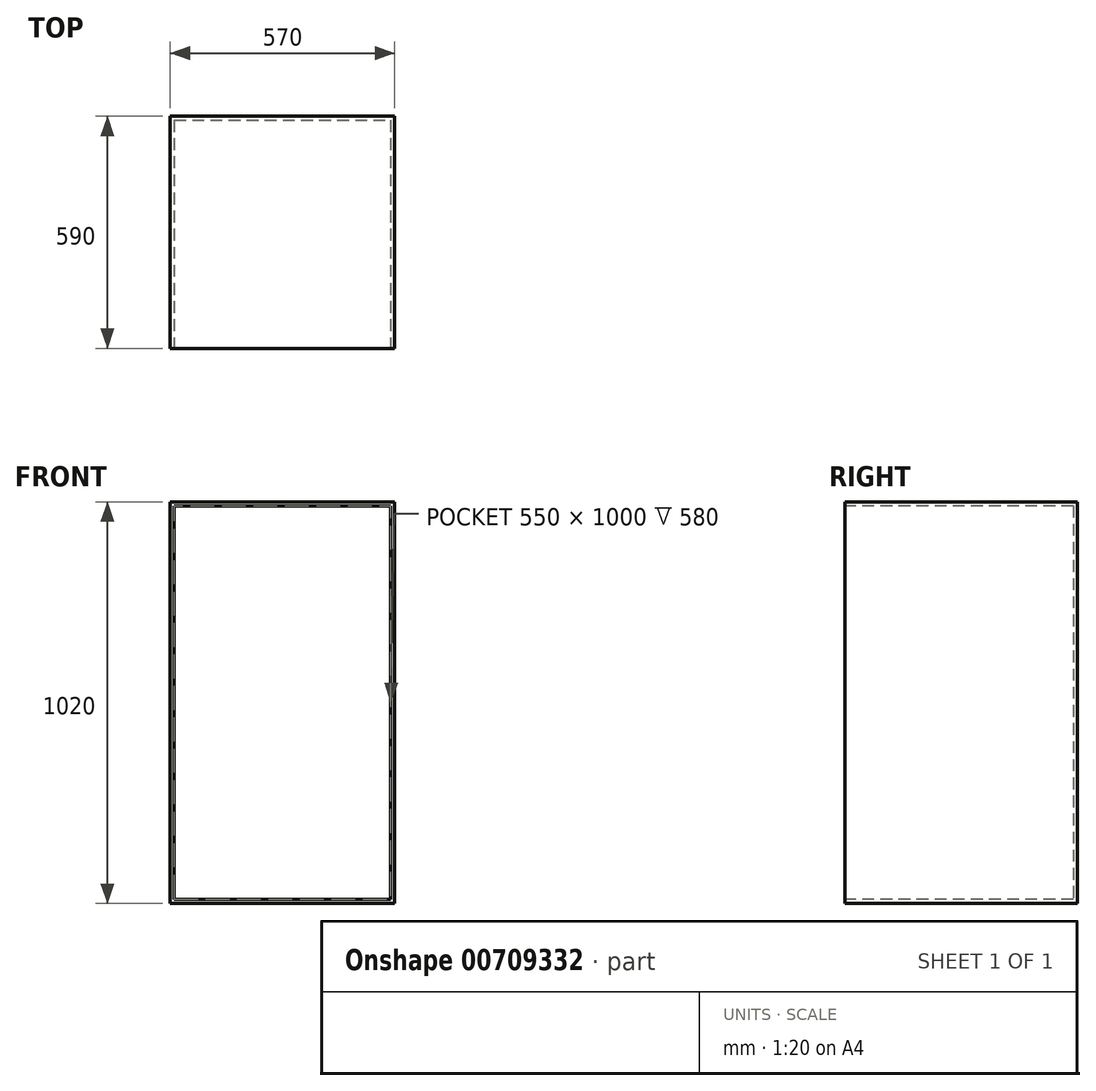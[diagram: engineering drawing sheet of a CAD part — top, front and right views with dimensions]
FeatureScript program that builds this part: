
annotation { "Feature Type Name" : "Feature", "Feature Type Description" : "" }
export const myFeature = defineFeature(function(context is Context, id is Id, definition is map)
    precondition{}
    {
        {
            var Q0;
            Q0=qCreatedBy(makeId("Top.planeOp"),FACE);
            var sketch = newSketch(context, id + "F0", { "sketchPlane" : qUnion([Q0])});
            skLineSegment(sketch, "E0.bottom", {"start": v(-275, 290) * mm, "end": v(275, 290) * mm});
            skLineSegment(sketch, "E0.top", {"start": v(-275, -290) * mm, "end": v(275, -290) * mm});
            skLineSegment(sketch, "E0.left", {"start": v(-275, 290) * mm, "end": v(-275, -290) * mm});
            skLineSegment(sketch, "E0.right", {"start": v(275, 290) * mm, "end": v(275, -290) * mm});
            skPoint(sketch, "E0.middle", {"position": v(0, 0) * mm});
            skSolve(sketch);
        }
        {
            var Q0;
            Q0=makeQuery(id+"F0.imprint","IMPRINT",FACE,{"disambiguationData":[TD([[makeQuery(id+"F0.imprint","IMPRINT",EDGE,{"derivedFrom":sQuery(id+"F0.wireOp",EDGE,"E0.bottom")}),-1.0]])]});
            extrude(context, id + "F1", {"entities" : qUnion([Q0]), "depth" : 1000 * mm, "offsetDistance" : 25 * mm});
        }
        {
            var Q0;
            Q0=makeQuery(id+"F1.opExtrude","SWEPT_FACE",FACE,{"disambiguationData":[OSD([sQuery(id+"F0.wireOp",EDGE,"E0.top")])]});
            shell(context, id + "F2", {"entities" : qUnion([Q0]), "thickness" : 10 * mm, "oppositeDirection" : true});
        }
    });
